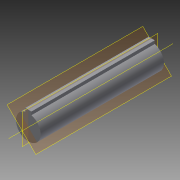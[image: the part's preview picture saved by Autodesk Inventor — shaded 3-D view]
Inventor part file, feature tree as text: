
AUTODESK INVENTOR PART (.ipt)
format: ipt  version: 2016 (Build 200138000, 138)  size: 83,968 bytes
history: native  units: in
note: dims shown in document units (in); Inventor stores cm internally (conversion verified against a paired STEP export)
features: plane x3, extrude x1, sketch x1
ambient origin geometry x8: Origin, YZ Plane, XZ Plane, XY Plane, X Axis, Y Axis, Z Axis, Center Point
bodies: Solid1 (feature_tree)
feature tree (5):
  extrude  "Extrusion1"  Depth=0.25in
  plane  "Work Plane1"
  plane  "Work Plane2"
  plane  "Work Plane3"
  sketch  "Sketch1"  dims[d0=1.0in d1=0.25in d2=0.13in d3=5.0in d4=0.0in d5=-0.3092in d6=45.0deg]
